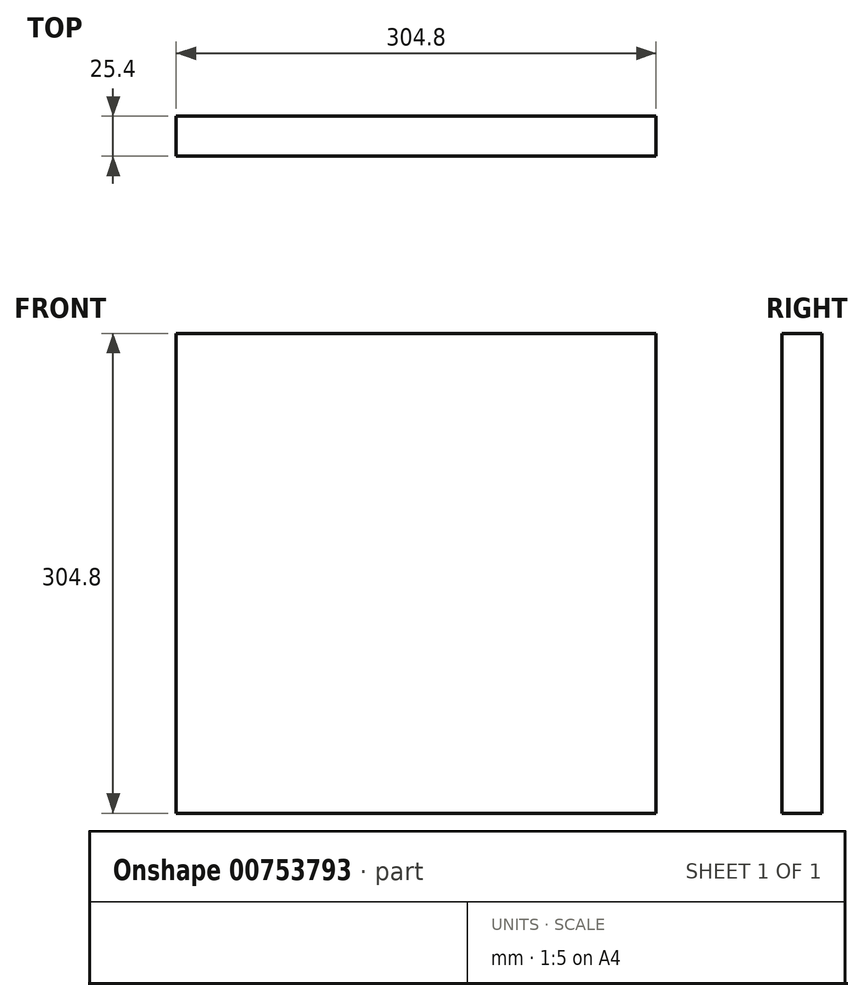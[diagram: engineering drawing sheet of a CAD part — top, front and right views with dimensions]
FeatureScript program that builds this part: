
annotation { "Feature Type Name" : "Feature", "Feature Type Description" : "" }
export const myFeature = defineFeature(function(context is Context, id is Id, definition is map)
    precondition{}
    {
        {
            var Q0;
            Q0=qCreatedBy(makeId("Front.planeOp"),FACE);
            var sketch = newSketch(context, id + "F0", { "sketchPlane" : qUnion([Q0])});
            skLineSegment(sketch, "E0.bottom", {"start": v(-261.9, 269.55) * mm, "end": v(42.9, 269.55) * mm});
            skLineSegment(sketch, "E0.top", {"start": v(-261.9, -35.25) * mm, "end": v(42.9, -35.25) * mm});
            skLineSegment(sketch, "E0.left", {"start": v(-261.9, 269.55) * mm, "end": v(-261.9, -35.25) * mm});
            skLineSegment(sketch, "E0.right", {"start": v(42.9, 269.55) * mm, "end": v(42.9, -35.25) * mm});
            skSolve(sketch);
        }
        {
            var Q0;
            Q0=makeQuery(id+"F0.imprint","IMPRINT",FACE,{"disambiguationData":[TD([[makeQuery(id+"F0.imprint","IMPRINT",EDGE,{"derivedFrom":sQuery(id+"F0.wireOp",EDGE,"E0.bottom")}),-1.0]])]});
            extrude(context, id + "F1", {"entities" : qUnion([Q0]), "depth" : 25.4 * mm, "offsetDistance" : 25.4 * mm});
        }
    });
